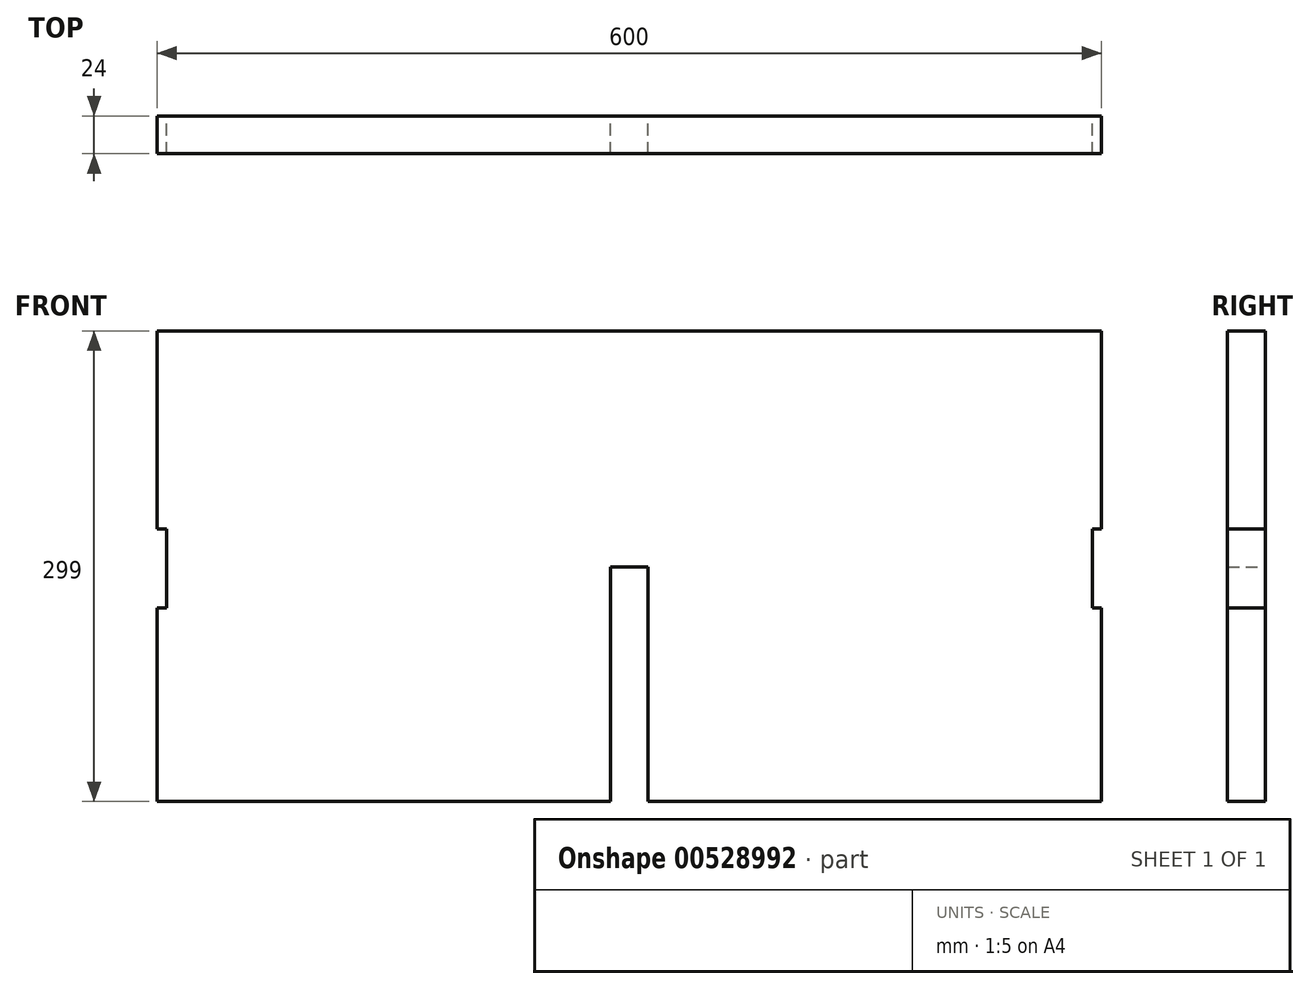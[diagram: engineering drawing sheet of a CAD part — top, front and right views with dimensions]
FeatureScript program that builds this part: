
annotation { "Feature Type Name" : "Feature", "Feature Type Description" : "" }
export const myFeature = defineFeature(function(context is Context, id is Id, definition is map)
    precondition{}
    {
        {
            var Q0;
            Q0=qCreatedBy(makeId("Front.planeOp"),FACE);
            var sketch = newSketch(context, id + "F0", { "sketchPlane" : qUnion([Q0])});
            skLineSegment(sketch, "E0.bottom", {"start": v(-369.5, 138) * mm, "end": v(230.5, 138) * mm});
            skLineSegment(sketch, "E0.top", {"start": v(-369.5, -161) * mm, "end": v(-81.5, -161) * mm});
            skLineSegment(sketch, "E0.left", {"start": v(-369.5, 138) * mm, "end": v(-369.5, -161) * mm});
            skLineSegment(sketch, "E0.right", {"start": v(230.5, 138) * mm, "end": v(230.5, -161) * mm});
            skLineSegment(sketch, "E1", {"start": v(-57.5, -12) * mm, "end": v(-57.5, -161) * mm});
            skLineSegment(sketch, "E2", {"start": v(-81.5, -12) * mm, "end": v(-81.5, -161) * mm});
            skLineSegment(sketch, "E3", {"start": v(-57.5, -12) * mm, "end": v(-81.5, -12) * mm});
            skLineSegment(sketch, "E4", {"start": v(-369.5, -38) * mm, "end": v(-363.5, -38) * mm});
            skLineSegment(sketch, "E5", {"start": v(-363.5, -38) * mm, "end": v(-363.5, 12) * mm});
            skLineSegment(sketch, "E6", {"start": v(-363.5, 12) * mm, "end": v(-369.5, 12) * mm});
            skLineSegment(sketch, "E7", {"start": v(230.5, 12) * mm, "end": v(224.5, 12) * mm});
            skLineSegment(sketch, "E8", {"start": v(224.5, 12) * mm, "end": v(224.5, -38) * mm});
            skLineSegment(sketch, "E9", {"start": v(224.5, -38) * mm, "end": v(230.5, -38) * mm});
            skLineSegment(sketch, "E10.trimOffspring", {"start": v(-57.5, -161) * mm, "end": v(230.5, -161) * mm});
            skSolve(sketch);
        }
        {
            var Q0;
            Q0 = qSketchRegion(id + "F0", true);
            extrude(context, id + "F1", {"entities" : qUnion([Q0]), "depth" : 24 * mm, "offsetDistance" : 25 * mm});
        }
        {
            var Q0;
            {var subQ0=sQuery(id+"F0.wireOp",EDGE,"E4");Q0=makeQuery(id+"F0.imprint","IMPRINT",FACE,{"disambiguationData":[TD([[makeQuery(id+"F0.imprint","IMPRINT",EDGE,{"derivedFrom":subQ0}),1.0]])]});}
            var Q1;
            {var subQ0=sQuery(id+"F0.wireOp",EDGE,"E7");Q1=makeQuery(id+"F0.imprint","IMPRINT",FACE,{"disambiguationData":[TD([[makeQuery(id+"F0.imprint","IMPRINT",EDGE,{"derivedFrom":subQ0}),1.0]])]});}
            extrude(context, id + "F2", {"entities" : qUnion([Q0, Q1]), "operationType" : NewBodyOperationType.REMOVE, "depth" : 96 * mm, "offsetDistance" : 25 * mm});
        }
    });
